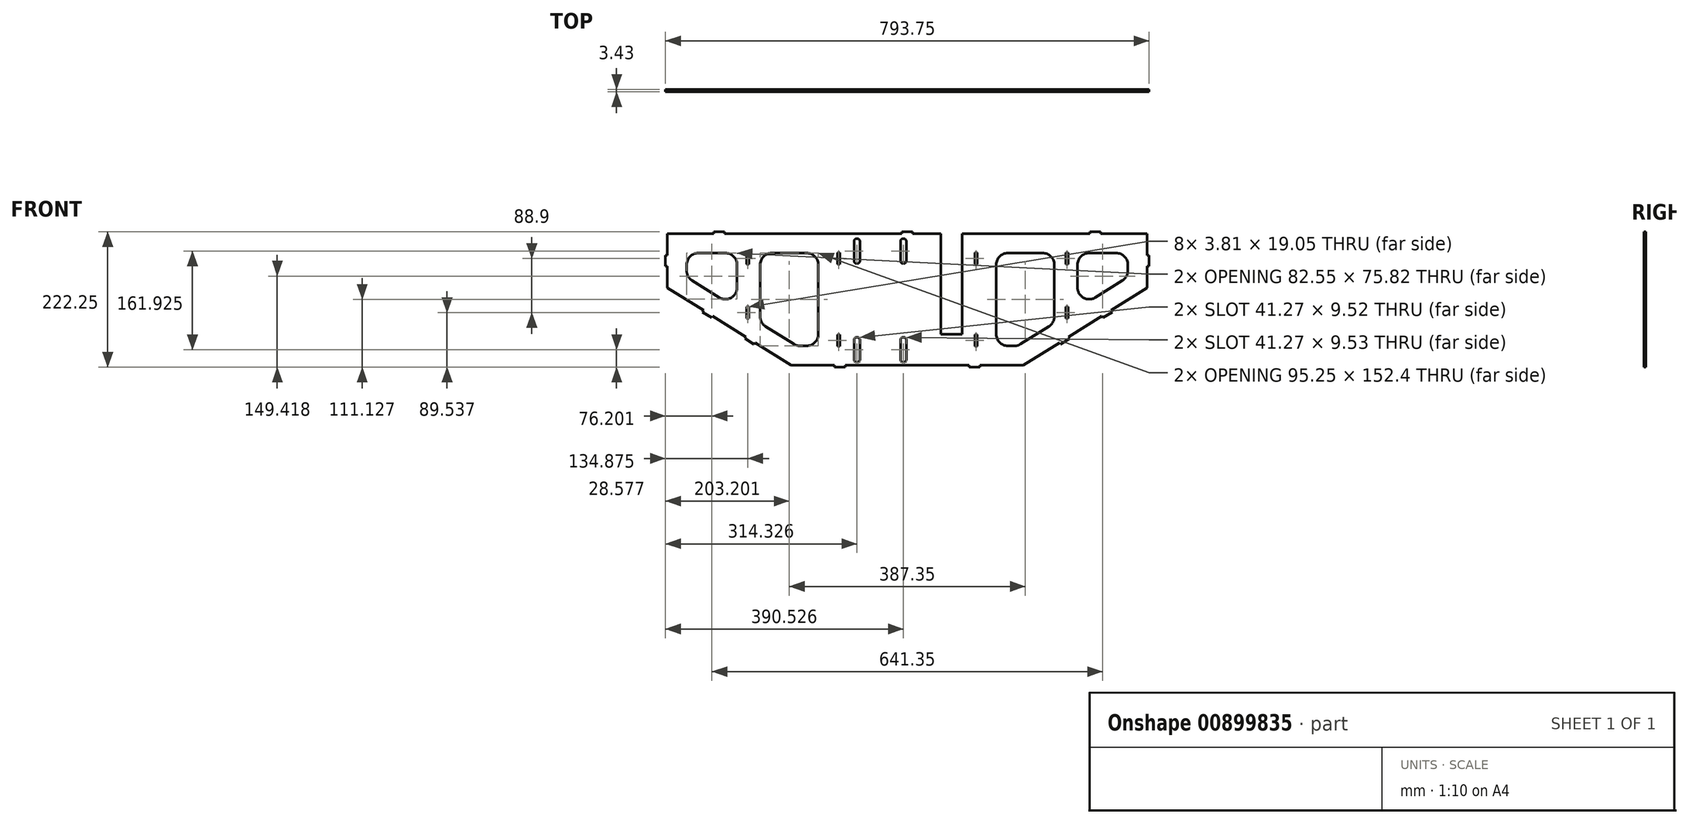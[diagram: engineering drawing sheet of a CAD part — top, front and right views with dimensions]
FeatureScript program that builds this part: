
annotation { "Feature Type Name" : "Feature", "Feature Type Description" : "" }
export const myFeature = defineFeature(function(context is Context, id is Id, definition is map)
    precondition{}
    {
        {
            var Q0;
            Q0=qCreatedBy(makeId("Front.planeOp"),FACE);
            var sketch = newSketch(context, id + "F0", { "sketchPlane" : qUnion([Q0])});
            skArc(sketch, "E0", {"start": v(757.8, -299.82) * mm, "mid": v(744.33, -305.4) * mm, "end": v(738.75, -318.87) * mm});
            skLineSegment(sketch, "E1", {"start": v(738.75, -318.87) * mm, "end": v(738.75, -356.6) * mm});
            skArc(sketch, "E2", {"start": v(738.75, -356.6) * mm, "mid": v(748.56, -373.26) * mm, "end": v(767.9, -372.75) * mm});
            skLineSegment(sketch, "E3", {"start": v(767.9, -372.75) * mm, "end": v(812.34, -344.97) * mm});
            skArc(sketch, "E4", {"start": v(812.34, -344.97) * mm, "mid": v(818.9, -338.05) * mm, "end": v(821.3, -328.82) * mm});
            skLineSegment(sketch, "E5", {"start": v(821.3, -328.82) * mm, "end": v(821.3, -318.87) * mm});
            skArc(sketch, "E6", {"start": v(821.3, -318.87) * mm, "mid": v(815.72, -305.4) * mm, "end": v(802.25, -299.82) * mm});
            skLineSegment(sketch, "E7", {"start": v(802.25, -299.82) * mm, "end": v(757.8, -299.82) * mm});
            skArc(sketch, "E8", {"start": v(381.56, -442.7) * mm, "mid": v(376.8, -437.94) * mm, "end": v(372.03, -442.7) * mm});
            skLineSegment(sketch, "E9", {"start": v(372.03, -474.45) * mm, "end": v(372.03, -442.7) * mm});
            skArc(sketch, "E10", {"start": v(372.03, -474.45) * mm, "mid": v(376.8, -479.21) * mm, "end": v(381.56, -474.45) * mm});
            skLineSegment(sketch, "E11", {"start": v(381.56, -442.7) * mm, "end": v(381.56, -474.45) * mm});
            skArc(sketch, "E12", {"start": v(381.56, -280.77) * mm, "mid": v(376.8, -276.01) * mm, "end": v(372.03, -280.77) * mm});
            skLineSegment(sketch, "E13", {"start": v(372.03, -312.52) * mm, "end": v(372.03, -280.77) * mm});
            skArc(sketch, "E14", {"start": v(372.03, -312.52) * mm, "mid": v(376.8, -317.29) * mm, "end": v(381.56, -312.52) * mm});
            skLineSegment(sketch, "E15", {"start": v(381.56, -280.77) * mm, "end": v(381.56, -312.52) * mm});
            skArc(sketch, "E16", {"start": v(448.23, -312.52) * mm, "mid": v(453, -317.29) * mm, "end": v(457.76, -312.52) * mm});
            skLineSegment(sketch, "E17", {"start": v(457.76, -280.77) * mm, "end": v(457.76, -312.52) * mm});
            skArc(sketch, "E18", {"start": v(457.76, -280.77) * mm, "mid": v(453, -276.01) * mm, "end": v(448.23, -280.77) * mm});
            skLineSegment(sketch, "E19", {"start": v(448.23, -312.52) * mm, "end": v(448.23, -280.77) * mm});
            skArc(sketch, "E20", {"start": v(448.23, -474.45) * mm, "mid": v(453, -479.21) * mm, "end": v(457.76, -474.45) * mm});
            skLineSegment(sketch, "E21", {"start": v(457.76, -442.7) * mm, "end": v(457.76, -474.45) * mm});
            skArc(sketch, "E22", {"start": v(457.76, -442.7) * mm, "mid": v(453, -437.94) * mm, "end": v(448.23, -442.7) * mm});
            skLineSegment(sketch, "E23", {"start": v(448.23, -474.45) * mm, "end": v(448.23, -442.7) * mm});
            skArc(sketch, "E24", {"start": v(218.05, -404.22) * mm, "mid": v(220.43, -413.46) * mm, "end": v(227, -420.38) * mm});
            skLineSegment(sketch, "E25", {"start": v(273.32, -449.33) * mm, "end": v(227, -420.38) * mm});
            skArc(sketch, "E26", {"start": v(273.32, -449.33) * mm, "mid": v(278.16, -451.48) * mm, "end": v(283.42, -452.22) * mm});
            skLineSegment(sketch, "E27", {"start": v(294.25, -452.22) * mm, "end": v(283.42, -452.22) * mm});
            skArc(sketch, "E28", {"start": v(294.25, -452.22) * mm, "mid": v(307.72, -446.64) * mm, "end": v(313.3, -433.17) * mm});
            skLineSegment(sketch, "E29", {"start": v(313.3, -318.87) * mm, "end": v(313.3, -433.17) * mm});
            skArc(sketch, "E30", {"start": v(313.3, -318.87) * mm, "mid": v(307.72, -305.4) * mm, "end": v(294.25, -299.82) * mm});
            skLineSegment(sketch, "E31", {"start": v(237.1, -299.82) * mm, "end": v(294.25, -299.82) * mm});
            skArc(sketch, "E32", {"start": v(237.1, -299.82) * mm, "mid": v(223.63, -305.4) * mm, "end": v(218.05, -318.87) * mm});
            skLineSegment(sketch, "E33", {"start": v(218.05, -404.22) * mm, "end": v(218.05, -318.87) * mm});
            skArc(sketch, "E34", {"start": v(150.8, -372.75) * mm, "mid": v(170.13, -373.26) * mm, "end": v(179.95, -356.6) * mm});
            skLineSegment(sketch, "E35", {"start": v(179.95, -318.87) * mm, "end": v(179.95, -356.6) * mm});
            skArc(sketch, "E36", {"start": v(179.95, -318.87) * mm, "mid": v(174.37, -305.4) * mm, "end": v(160.9, -299.82) * mm});
            skLineSegment(sketch, "E37", {"start": v(116.45, -299.82) * mm, "end": v(160.9, -299.82) * mm});
            skArc(sketch, "E38", {"start": v(116.45, -299.82) * mm, "mid": v(102.98, -305.4) * mm, "end": v(97.4, -318.87) * mm});
            skLineSegment(sketch, "E39", {"start": v(97.4, -328.82) * mm, "end": v(97.4, -318.87) * mm});
            skArc(sketch, "E40", {"start": v(97.4, -328.82) * mm, "mid": v(99.78, -338.05) * mm, "end": v(106.35, -344.97) * mm});
            skLineSegment(sketch, "E41", {"start": v(150.8, -372.75) * mm, "end": v(106.35, -344.97) * mm});
            skArc(sketch, "E42", {"start": v(605.4, -433.17) * mm, "mid": v(610.98, -446.64) * mm, "end": v(624.45, -452.22) * mm});
            skLineSegment(sketch, "E43", {"start": v(624.45, -452.22) * mm, "end": v(635.28, -452.22) * mm});
            skArc(sketch, "E44", {"start": v(635.28, -452.22) * mm, "mid": v(640.53, -451.48) * mm, "end": v(645.37, -449.33) * mm});
            skLineSegment(sketch, "E45", {"start": v(645.37, -449.33) * mm, "end": v(691.7, -420.38) * mm});
            skArc(sketch, "E46", {"start": v(691.7, -420.38) * mm, "mid": v(698.26, -413.46) * mm, "end": v(700.65, -404.22) * mm});
            skLineSegment(sketch, "E47", {"start": v(700.65, -404.22) * mm, "end": v(700.65, -318.87) * mm});
            skArc(sketch, "E48", {"start": v(700.65, -318.87) * mm, "mid": v(695.07, -305.4) * mm, "end": v(681.6, -299.82) * mm});
            skLineSegment(sketch, "E49", {"start": v(681.6, -299.82) * mm, "end": v(624.45, -299.82) * mm});
            skArc(sketch, "E50", {"start": v(624.45, -299.82) * mm, "mid": v(610.98, -305.4) * mm, "end": v(605.4, -318.87) * mm});
            skLineSegment(sketch, "E51", {"start": v(605.4, -318.87) * mm, "end": v(605.4, -433.17) * mm});
            skLineSegment(sketch, "E52", {"start": v(62.47, -303.63) * mm, "end": v(62.47, -321.41) * mm});
            skLineSegment(sketch, "E53", {"start": v(65.65, -303.63) * mm, "end": v(62.47, -303.63) * mm});
            skLineSegment(sketch, "E54", {"start": v(65.65, -268.07) * mm, "end": v(65.65, -303.63) * mm});
            skLineSegment(sketch, "E55", {"start": v(141.85, -268.07) * mm, "end": v(65.65, -268.07) * mm});
            skLineSegment(sketch, "E56", {"start": v(141.85, -264.9) * mm, "end": v(141.85, -268.07) * mm});
            skLineSegment(sketch, "E57", {"start": v(159.63, -264.9) * mm, "end": v(141.85, -264.9) * mm});
            skLineSegment(sketch, "E58", {"start": v(159.63, -268.07) * mm, "end": v(159.63, -264.9) * mm});
            skLineSegment(sketch, "E59", {"start": v(450.46, -268.07) * mm, "end": v(159.63, -268.07) * mm});
            skLineSegment(sketch, "E60", {"start": v(450.46, -264.9) * mm, "end": v(450.46, -268.07) * mm});
            skLineSegment(sketch, "E61", {"start": v(468.24, -264.9) * mm, "end": v(450.46, -264.9) * mm});
            skLineSegment(sketch, "E62", {"start": v(468.24, -268.07) * mm, "end": v(468.24, -264.9) * mm});
            skLineSegment(sketch, "E63", {"start": v(514.6, -268.07) * mm, "end": v(468.24, -268.07) * mm});
            skLineSegment(sketch, "E64", {"start": v(514.6, -268.07) * mm, "end": v(514.6, -433.17) * mm});
            skLineSegment(sketch, "E65", {"start": v(514.6, -433.17) * mm, "end": v(549.52, -433.17) * mm});
            skLineSegment(sketch, "E66", {"start": v(549.52, -433.17) * mm, "end": v(549.52, -268.07) * mm});
            skLineSegment(sketch, "E67", {"start": v(759.07, -268.07) * mm, "end": v(549.52, -268.07) * mm});
            skLineSegment(sketch, "E68", {"start": v(759.07, -264.9) * mm, "end": v(759.07, -268.07) * mm});
            skLineSegment(sketch, "E69", {"start": v(776.85, -264.9) * mm, "end": v(759.07, -264.9) * mm});
            skLineSegment(sketch, "E70", {"start": v(776.85, -268.07) * mm, "end": v(776.85, -264.9) * mm});
            skLineSegment(sketch, "E71", {"start": v(853.05, -268.07) * mm, "end": v(776.85, -268.07) * mm});
            skLineSegment(sketch, "E72", {"start": v(853.05, -303.63) * mm, "end": v(853.05, -268.07) * mm});
            skLineSegment(sketch, "E73", {"start": v(856.22, -303.63) * mm, "end": v(853.05, -303.63) * mm});
            skLineSegment(sketch, "E74", {"start": v(856.22, -321.41) * mm, "end": v(856.22, -303.63) * mm});
            skLineSegment(sketch, "E75", {"start": v(853.05, -321.41) * mm, "end": v(856.22, -321.41) * mm});
            skLineSegment(sketch, "E76", {"start": v(853.05, -356.97) * mm, "end": v(853.05, -321.41) * mm});
            skLineSegment(sketch, "E77", {"start": v(793.81, -394) * mm, "end": v(853.05, -356.97) * mm});
            skLineSegment(sketch, "E78", {"start": v(795.5, -396.69) * mm, "end": v(793.81, -394) * mm});
            skLineSegment(sketch, "E79", {"start": v(780.42, -406.1) * mm, "end": v(795.5, -396.69) * mm});
            skLineSegment(sketch, "E80", {"start": v(778.74, -403.42) * mm, "end": v(780.42, -406.1) * mm});
            skLineSegment(sketch, "E81", {"start": v(724.16, -437.53) * mm, "end": v(778.74, -403.42) * mm});
            skLineSegment(sketch, "E82", {"start": v(725.84, -440.22) * mm, "end": v(724.16, -437.53) * mm});
            skLineSegment(sketch, "E83", {"start": v(710.76, -449.64) * mm, "end": v(725.84, -440.22) * mm});
            skLineSegment(sketch, "E84", {"start": v(709.08, -446.95) * mm, "end": v(710.76, -449.64) * mm});
            skLineSegment(sketch, "E85", {"start": v(649.85, -483.97) * mm, "end": v(709.08, -446.95) * mm});
            skLineSegment(sketch, "E86", {"start": v(578.73, -487.15) * mm, "end": v(578.73, -483.97) * mm});
            skLineSegment(sketch, "E87", {"start": v(560.95, -487.15) * mm, "end": v(578.73, -487.15) * mm});
            skLineSegment(sketch, "E88", {"start": v(560.95, -483.97) * mm, "end": v(560.95, -487.15) * mm});
            skLineSegment(sketch, "E89", {"start": v(357.75, -483.97) * mm, "end": v(560.95, -483.97) * mm});
            skLineSegment(sketch, "E90", {"start": v(357.75, -487.15) * mm, "end": v(357.75, -483.97) * mm});
            skLineSegment(sketch, "E91", {"start": v(339.97, -487.15) * mm, "end": v(357.75, -487.15) * mm});
            skLineSegment(sketch, "E92", {"start": v(339.97, -483.97) * mm, "end": v(339.97, -487.15) * mm});
            skLineSegment(sketch, "E93", {"start": v(268.85, -483.97) * mm, "end": v(339.97, -483.97) * mm});
            skLineSegment(sketch, "E94", {"start": v(209.61, -446.95) * mm, "end": v(268.85, -483.97) * mm});
            skLineSegment(sketch, "E95", {"start": v(207.93, -449.64) * mm, "end": v(209.61, -446.95) * mm});
            skLineSegment(sketch, "E96", {"start": v(192.85, -440.22) * mm, "end": v(207.93, -449.64) * mm});
            skLineSegment(sketch, "E97", {"start": v(194.54, -437.53) * mm, "end": v(192.85, -440.22) * mm});
            skLineSegment(sketch, "E98", {"start": v(139.96, -403.42) * mm, "end": v(194.54, -437.53) * mm});
            skLineSegment(sketch, "E99", {"start": v(138.27, -406.1) * mm, "end": v(139.96, -403.42) * mm});
            skLineSegment(sketch, "E100", {"start": v(123.2, -396.69) * mm, "end": v(138.27, -406.1) * mm});
            skLineSegment(sketch, "E101", {"start": v(124.88, -394) * mm, "end": v(123.2, -396.69) * mm});
            skLineSegment(sketch, "E102", {"start": v(65.65, -356.97) * mm, "end": v(124.88, -394) * mm});
            skLineSegment(sketch, "E103", {"start": v(65.65, -321.41) * mm, "end": v(65.65, -356.97) * mm});
            skLineSegment(sketch, "E104", {"start": v(62.47, -321.41) * mm, "end": v(65.65, -321.41) * mm});
            skLineSegment(sketch, "E105", {"start": v(199.25, -299.19) * mm, "end": v(199.25, -318.24) * mm});
            skLineSegment(sketch, "E106", {"start": v(195.44, -299.19) * mm, "end": v(199.25, -299.19) * mm});
            skLineSegment(sketch, "E107", {"start": v(195.44, -318.24) * mm, "end": v(195.44, -299.19) * mm});
            skLineSegment(sketch, "E108", {"start": v(199.25, -318.24) * mm, "end": v(195.44, -318.24) * mm});
            skLineSegment(sketch, "E109", {"start": v(199.25, -388.09) * mm, "end": v(199.25, -407.14) * mm});
            skLineSegment(sketch, "E110", {"start": v(195.44, -388.09) * mm, "end": v(199.25, -388.09) * mm});
            skLineSegment(sketch, "E111", {"start": v(195.44, -407.14) * mm, "end": v(195.44, -388.09) * mm});
            skLineSegment(sketch, "E112", {"start": v(199.25, -407.14) * mm, "end": v(195.44, -407.14) * mm});
            skLineSegment(sketch, "E113", {"start": v(348.6, -433.8) * mm, "end": v(348.6, -452.86) * mm});
            skLineSegment(sketch, "E114", {"start": v(344.8, -433.8) * mm, "end": v(348.6, -433.8) * mm});
            skLineSegment(sketch, "E115", {"start": v(344.8, -452.86) * mm, "end": v(344.8, -433.8) * mm});
            skLineSegment(sketch, "E116", {"start": v(348.6, -452.86) * mm, "end": v(344.8, -452.86) * mm});
            skLineSegment(sketch, "E117", {"start": v(348.6, -299.19) * mm, "end": v(348.6, -318.24) * mm});
            skLineSegment(sketch, "E118", {"start": v(344.8, -299.19) * mm, "end": v(348.6, -299.19) * mm});
            skLineSegment(sketch, "E119", {"start": v(344.8, -318.24) * mm, "end": v(344.8, -299.19) * mm});
            skLineSegment(sketch, "E120", {"start": v(348.6, -318.24) * mm, "end": v(344.8, -318.24) * mm});
            skLineSegment(sketch, "E121", {"start": v(573.9, -318.24) * mm, "end": v(570.09, -318.24) * mm});
            skLineSegment(sketch, "E122", {"start": v(573.9, -299.19) * mm, "end": v(573.9, -318.24) * mm});
            skLineSegment(sketch, "E123", {"start": v(570.09, -299.19) * mm, "end": v(573.9, -299.19) * mm});
            skLineSegment(sketch, "E124", {"start": v(570.09, -318.24) * mm, "end": v(570.09, -299.19) * mm});
            skLineSegment(sketch, "E125", {"start": v(573.9, -452.86) * mm, "end": v(570.09, -452.86) * mm});
            skLineSegment(sketch, "E126", {"start": v(573.9, -433.8) * mm, "end": v(573.9, -452.86) * mm});
            skLineSegment(sketch, "E127", {"start": v(570.09, -433.8) * mm, "end": v(573.9, -433.8) * mm});
            skLineSegment(sketch, "E128", {"start": v(570.09, -452.86) * mm, "end": v(570.09, -433.8) * mm});
            skLineSegment(sketch, "E129", {"start": v(723.25, -407.14) * mm, "end": v(719.44, -407.14) * mm});
            skLineSegment(sketch, "E130", {"start": v(723.25, -388.09) * mm, "end": v(723.25, -407.14) * mm});
            skLineSegment(sketch, "E131", {"start": v(719.44, -388.09) * mm, "end": v(723.25, -388.09) * mm});
            skLineSegment(sketch, "E132", {"start": v(719.44, -407.14) * mm, "end": v(719.44, -388.09) * mm});
            skLineSegment(sketch, "E133", {"start": v(723.25, -318.24) * mm, "end": v(719.44, -318.24) * mm});
            skLineSegment(sketch, "E134", {"start": v(723.25, -299.19) * mm, "end": v(723.25, -318.24) * mm});
            skLineSegment(sketch, "E135", {"start": v(719.44, -299.19) * mm, "end": v(723.25, -299.19) * mm});
            skLineSegment(sketch, "E136", {"start": v(719.44, -318.24) * mm, "end": v(719.44, -299.19) * mm});
            skLineSegment(sketch, "E137", {"start": v(578.73, -483.97) * mm, "end": v(649.85, -483.97) * mm});
            skSolve(sketch);
        }
        {
            var Q0;
            Q0 = qSketchRegion(id + "F0", true);
            extrude(context, id + "F1", {"entities" : qUnion([Q0]), "depth" : 3.43 * mm, "offsetDistance" : 25.4 * mm});
        }
    });
